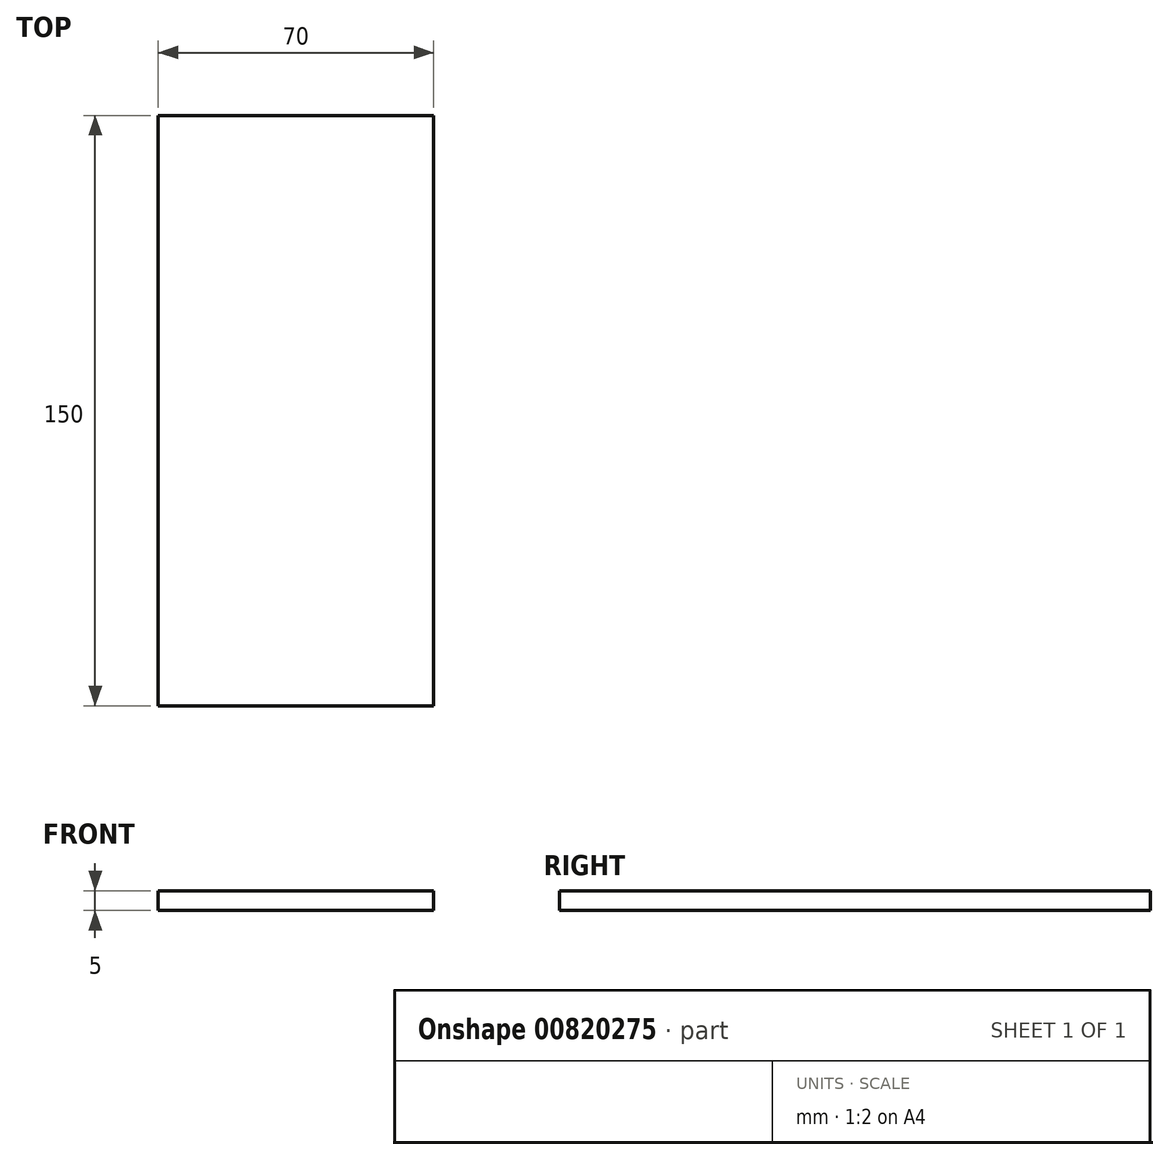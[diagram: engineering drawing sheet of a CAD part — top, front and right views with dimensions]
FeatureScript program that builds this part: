
annotation { "Feature Type Name" : "Feature", "Feature Type Description" : "" }
export const myFeature = defineFeature(function(context is Context, id is Id, definition is map)
    precondition{}
    {
        {
            var Q0;
            Q0=qCreatedBy(makeId("Top.planeOp"),FACE);
            var sketch = newSketch(context, id + "F0", { "sketchPlane" : qUnion([Q0])});
            skLineSegment(sketch, "E0.bottom", {"start": v(-27.65, 118.69) * mm, "end": v(42.35, 118.69) * mm});
            skLineSegment(sketch, "E0.top", {"start": v(-27.65, -31.31) * mm, "end": v(42.35, -31.31) * mm});
            skLineSegment(sketch, "E0.left", {"start": v(-27.65, 118.69) * mm, "end": v(-27.65, -31.31) * mm});
            skLineSegment(sketch, "E0.right", {"start": v(42.35, 118.69) * mm, "end": v(42.35, -31.31) * mm});
            skSolve(sketch);
        }
        {
            var Q0;
            Q0 = qSketchRegion(id + "F0", true);
            extrude(context, id + "F1", {"entities" : qUnion([Q0]), "depth" : 5 * mm, "offsetDistance" : 25 * mm});
        }
    });
